# Revit family: Circuit-Breaker-Panel
name_source: partatom
category: Electrical Fixtures
units: mm (PartAtom-declared; Revit-internal decimal feet)

## family parameters
Always vertical = Yes
Classification Number = 23.80.40.14
Cut with Voids When Loaded = No
Host = Wall
Maintain Annotation Orientation = No
Part Type = Normal
Room Calculation Point = No
Round Connector Dimension = Use Diameter
Shared = No

## types (2) — shared parameters
Assembly Code = D5010200
Building Codes = http://www.nfpa.org
Circuit 6 - (NAME) = 10
Circuit 9 - (NAME) = 15
Construction Details = http://www.arcat.com
Default Elevation = 0' - 0"
Description = 200A Electrical Service Panel
Expected Lifespan (Years) = 50
Green Building-LEED = http://www.arcat.com
Gross Depth = 0' - 3 1/2"
Gross Projection = 0' - 0 1/4"
Gross Width = 1' - 4 1/2"
Installation Phase = Rough Electrical
Keynote = 16410
Lug Count = 40
Maintainence Schedule (Months) = 24
Manufacturer = Generic
Manufacturer Fax = (203) 939-2444
Manufacturer Website = http://www.arcat.com
Model = Generic
Product Data = http://www.arcat.com
Product Properties = http://www.arcat.com
Specification = http://www.arcat.com
Type Comments = 200A Electrical Service Panel
UL Listed = Yes
Warranty Duration (Years) = 2

## per-type parameters (varying)
| type | CircArray | Circuit 1 - (NAME) | Circuit 2 - (NAME) | Circuit 3 - (NAME) | Circuit 4 - (NAME) | Circuit 5 - (NAME) | Circuit 7 - (NAME) | Circuit 8 - (NAME) | Gross Height | Maximum Amps | Mounting Height | bbheight |
| 200A Panel | 20 | 10 | 15 | 10 | 30 | 20 | 20 | 10 | 2' - 6" | 200 | 6' - 0" | 1' - 8" |
| 100A Panel | 10 | 20 | 10 | 15 | 10 | 30 | 10 | 20 | 1' - 4" | 100 | 5' - 0" | 0' - 10" |

## geometry (parser evidence)
native form markers: Sweep x5
no freeform markers — native parametric forms only
